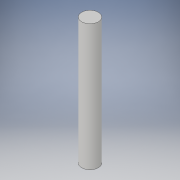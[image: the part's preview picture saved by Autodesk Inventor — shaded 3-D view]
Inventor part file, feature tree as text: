
AUTODESK INVENTOR PART (.ipt)
format: ipt  version: 2019 (Build 230136000, 136)  size: 89,600 bytes
history: native  units: mm
features: extrude x1, sketch x1
ambient origin geometry x8: Origin, YZ Plane, XZ Plane, XY Plane, X Axis, Y Axis, Z Axis, Center Point
bodies: Solid1 (feature_tree)
feature tree (2):
  extrude  "Extrusion1"  Depth=76.0mm TaperAngle=0.0deg
  sketch  "Sketch1"  dims[d0=10.0mm d1=76.0mm d2=0.0mm]
